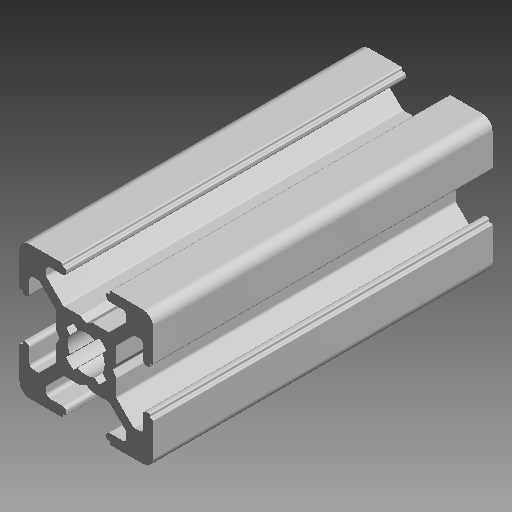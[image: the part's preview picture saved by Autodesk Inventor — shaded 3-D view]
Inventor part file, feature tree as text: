
AUTODESK INVENTOR PART (.ipt)
format: ipt  version: 2019 (Build 230136000, 136)  size: 389,120 bytes
history: native  units: mm (DEFAULTED — no unit token found)
features: other x5, sketch x1
ambient origin geometry x8: Origin, YZ Plane, XZ Plane, XY Plane, X Axis, Y Axis, Z Axis, Center Point
bodies: Solid1 (feature_tree)
feature tree (6):
  other  "Bosch 20x20 - 4.5 Part.Shoot.ipt"
  other  "Blocks"
  other  "20x20"
  other  "Solid1::Bosch 20x20 - 4.5 Part.Shoot.ipt"
  other  "TaggingFeature1"
  sketch  "Sketch1"  dims[d0=10.0mm]
